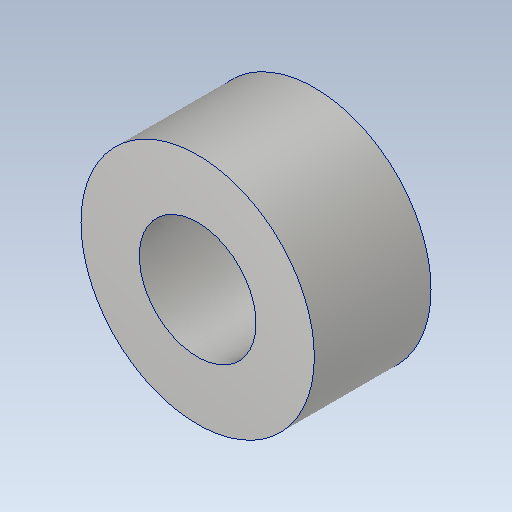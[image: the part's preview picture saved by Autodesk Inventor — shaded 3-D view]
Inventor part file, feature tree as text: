
AUTODESK INVENTOR PART (.ipt)
format: ipt  version: 2020.2 (Build 242310000, 310)  size: 109,056 bytes
history: native  units: mm
features: other x1, extrude x1, sketch x1
ambient origin geometry x8: Origin, YZ Plane, XZ Plane, XY Plane, X Axis, Y Axis, Z Axis, Center Point
bodies: Body1 (feature_tree)
feature tree (3):
  other  "ソリッド1"
  extrude  "押し出し1"  Depth=6.0mm
  sketch  "スケッチ1"
